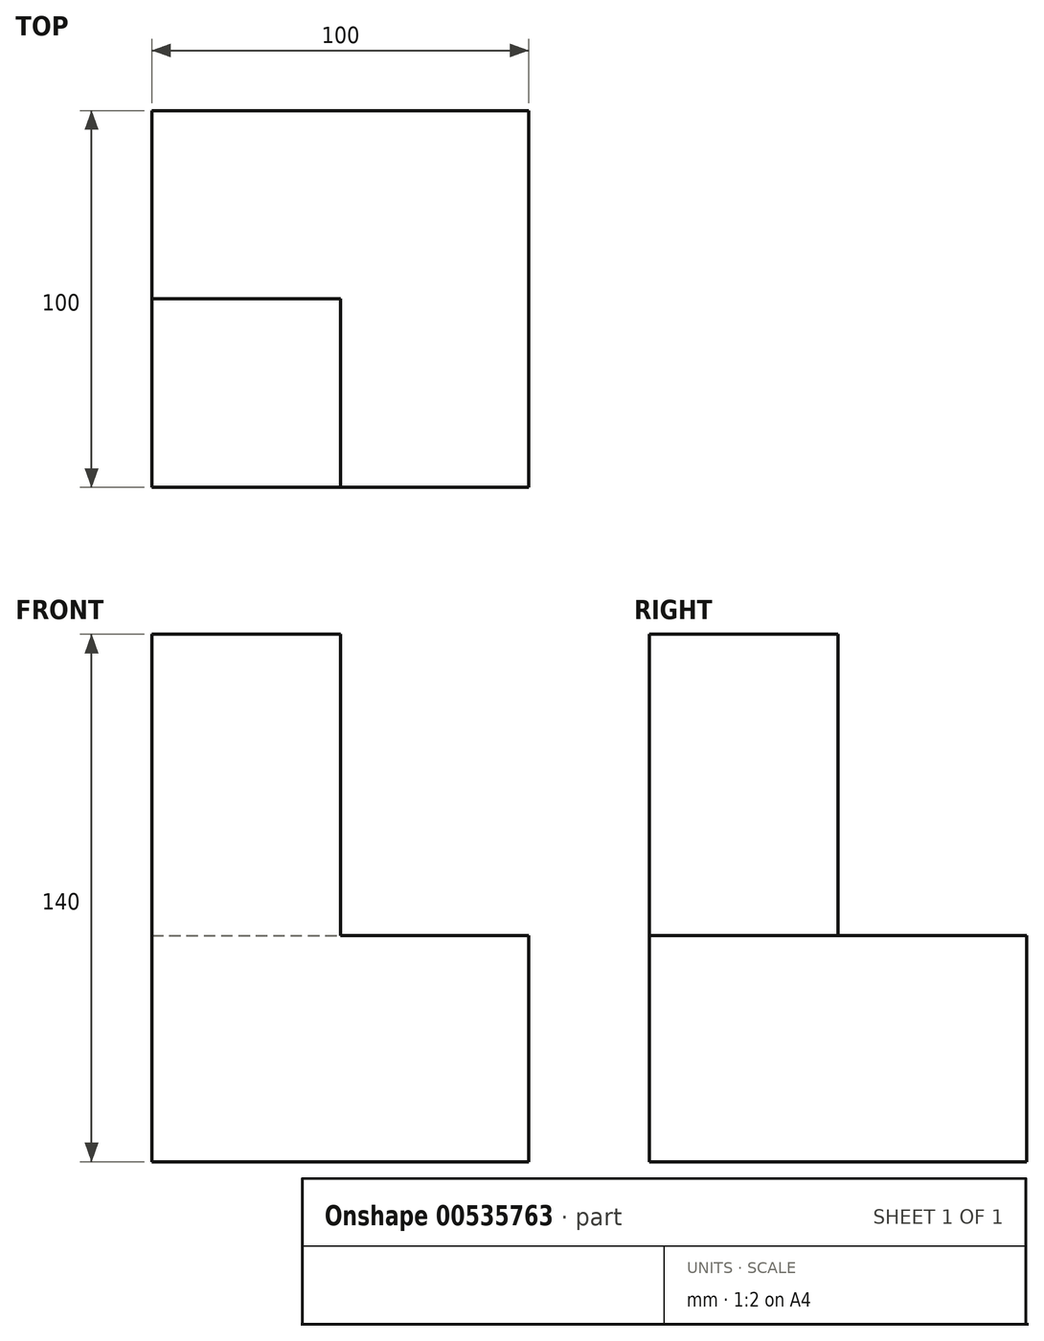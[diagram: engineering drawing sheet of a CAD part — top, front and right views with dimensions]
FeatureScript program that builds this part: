
annotation { "Feature Type Name" : "Feature", "Feature Type Description" : "" }
export const myFeature = defineFeature(function(context is Context, id is Id, definition is map)
    precondition{}
    {
        {
            var Q0;
            Q0=qCreatedBy(makeId("Top.planeOp"),FACE);
            var sketch = newSketch(context, id + "F0", { "sketchPlane" : qUnion([Q0])});
            skLineSegment(sketch, "E0.bottom", {"start": v(-58.82, 60.23) * mm, "end": v(41.18, 60.23) * mm});
            skLineSegment(sketch, "E0.top", {"start": v(-58.82, -39.77) * mm, "end": v(41.18, -39.77) * mm});
            skLineSegment(sketch, "E0.left", {"start": v(-58.82, 60.23) * mm, "end": v(-58.82, -39.77) * mm});
            skLineSegment(sketch, "E0.right", {"start": v(41.18, 60.23) * mm, "end": v(41.18, -39.77) * mm});
            skSolve(sketch);
        }
        {
            var Q0;
            Q0 = qSketchRegion(id + "F0", true);
            extrude(context, id + "F1", {"entities" : qUnion([Q0]), "depth" : 140 * mm, "offsetDistance" : 25 * mm});
        }
        {
            var Q0;
            Q0=makeQuery(id+"F1.opExtrude","SWEPT_FACE",FACE,{"disambiguationData":[OSD([sQuery(id+"F0.wireOp",EDGE,"E0.top")])]});
            var sketch = newSketch(context, id + "F2", { "sketchPlane" : qUnion([Q0])});
            skLineSegment(sketch, "E1.bottom", {"start": v(-8.82, 140) * mm, "end": v(41.18, 140) * mm});
            skLineSegment(sketch, "E1.top", {"start": v(-8.82, 60) * mm, "end": v(41.18, 60) * mm});
            skLineSegment(sketch, "E1.left", {"start": v(-8.82, 140) * mm, "end": v(-8.82, 60) * mm});
            skLineSegment(sketch, "E1.right", {"start": v(41.18, 140) * mm, "end": v(41.18, 60) * mm});
            skSolve(sketch);
        }
        {
            var Q0;
            Q0 = qSketchRegion(id + "F2", true);
            extrude(context, id + "F3", {"entities" : qUnion([Q0]), "operationType" : NewBodyOperationType.REMOVE, "endBound" : BoundingType.UP_TO_NEXT, "oppositeDirection" : true, "depth" : 25 * mm, "offsetDistance" : 25 * mm});
        }
        {
            var Q0;
            Q0=makeQuery(id+"F3.boolean.opBoolean","COPY",FACE,{"derivedFrom":makeQuery(id+"F3.opExtrude","SWEPT_FACE",FACE,{"disambiguationData":[OSD([sQuery(id+"F2.wireOp",EDGE,"E1.left")])]})});
            var sketch = newSketch(context, id + "F4", { "sketchPlane" : qUnion([Q0])});
            skLineSegment(sketch, "E2.bottom", {"start": v(10.23, 140) * mm, "end": v(60.23, 140) * mm});
            skLineSegment(sketch, "E2.top", {"start": v(10.23, 60) * mm, "end": v(60.23, 60) * mm});
            skLineSegment(sketch, "E2.left", {"start": v(10.23, 140) * mm, "end": v(10.23, 60) * mm});
            skLineSegment(sketch, "E2.right", {"start": v(60.23, 140) * mm, "end": v(60.23, 60) * mm});
            skSolve(sketch);
        }
        {
            var Q0;
            Q0 = qSketchRegion(id + "F4", true);
            extrude(context, id + "F5", {"entities" : qUnion([Q0]), "operationType" : NewBodyOperationType.REMOVE, "endBound" : BoundingType.UP_TO_NEXT, "oppositeDirection" : true, "depth" : 25 * mm, "offsetDistance" : 25 * mm});
        }
    });
